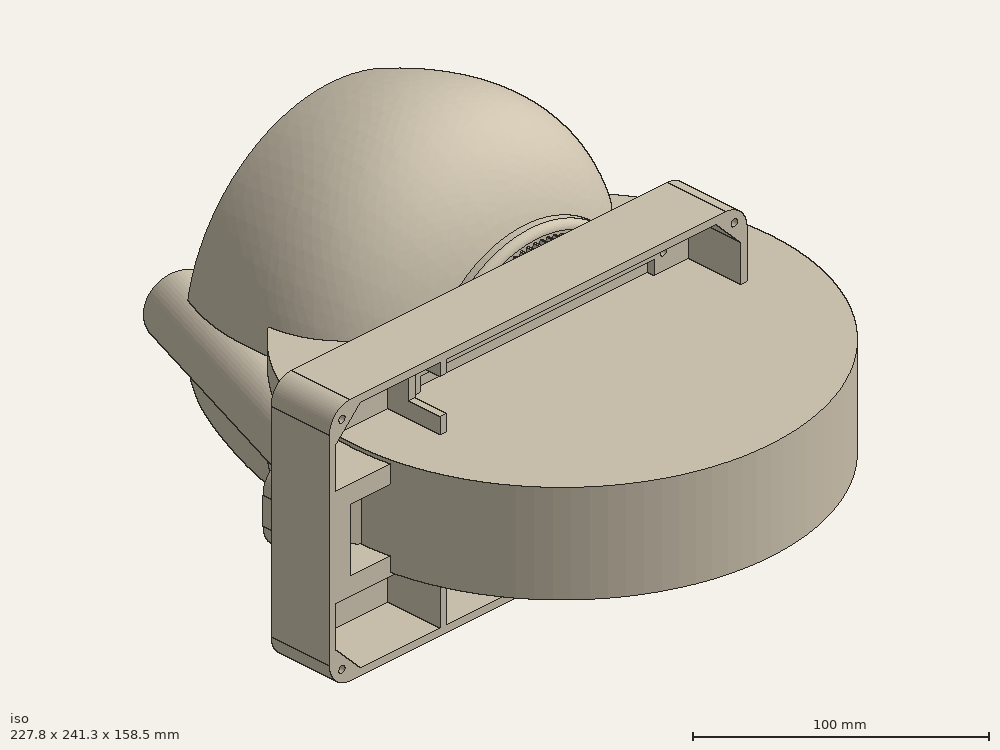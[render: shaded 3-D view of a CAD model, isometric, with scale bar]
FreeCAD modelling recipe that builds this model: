
FCSTD DOCUMENT  (FreeCAD 0.21R33771 (Git))
Label: hello_bowl
License: All rights reserved
LicenseURL: https://en.wikipedia.org/wiki/All_rights_reserved
objects: Sketcher::SketchObject×38, PartDesign::Pocket×19, PartDesign::Pad×17, PartDesign::Body×14, PartDesign::Fillet×12, Mesh::Feature×8, Part::Feature×3, PartDesign::Revolution×2, PartDesign::PolarPattern×2, PartDesign::FeaturePython×2, Part::Part2DObjectPython×1, Part::Cylinder×1, Part::Cut×1
note: 162 computed .brp shape members not serialized (recipe doc carries the construction recipe); baked Part::Feature solids carry a one-line shape summary decoded from their .brp

FEATURE [Mesh::Feature] _  label="2"
  Placement = pos=(-60.5739,41.9909,16.8) rot=(0.990267,0.001215,0.139173;3.15888rad)
FEATURE [Mesh::Feature] _001  label="1"
  Placement = pos=(-57.21,43.02,-7.46) rot=(0,0,1;0rad)
FEATURE [Mesh::Feature] motor
  Placement = pos=(-51.81,-45.18,0) rot=(0,1,0;2.32129rad)
FEATURE [Mesh::Feature] Motor_Gear
  Placement = pos=(-53.5,108.6,-21.24) rot=(0,0,1;0rad)
FEATURE [Mesh::Feature] Base
  Placement = pos=(0,0,0) rot=(1,0,0;3.14159rad)
FEATURE [Mesh::Feature] Top_plate_
  Placement = pos=(9.04249,-243.781,-2.54) rot=(0,0,1;0.087266rad)
FEATURE [Sketcher::SketchObject] Sketch002
  FullyConstrained = true
  MapMode = 5
  Support = -> [XY_Plane001]
  sketch-geometry (1):
    g0: Circle CenterX=0 CenterY=0 CenterZ=0 NormalX=0 NormalY=0 NormalZ=1 AngleXU=0 Radius=100
  constraints (2):
    c: Coincident(g0,g-1)
    c: Diameter(g0) = 200
FEATURE [PartDesign::Pad] Pad001
  Direction = (0,0,1)
  Length = 44
  Length2 = 10
  Profile = -> Sketch002
  ReferenceAxis = -> Sketch002 [N_Axis]
  Type = 0
FEATURE [Sketcher::SketchObject] Sketch003
  FullyConstrained = true
  MapMode = 5
  Support = -> [XY_Plane001]
  sketch-geometry (2):
    g0: Circle CenterX=0 CenterY=0 CenterZ=0 NormalX=0 NormalY=0 NormalZ=1 AngleXU=0 Radius=98.5
    g1: Circle CenterX=0 CenterY=0 CenterZ=0 NormalX=0 NormalY=0 NormalZ=1 AngleXU=0 Radius=10
  constraints (4):
    c: Coincident(g0,g-1)
    c: Diameter(g0) = 197
    c: Coincident(g1,g0)
    c: Diameter(g1) = 20
FEATURE [PartDesign::Pocket] Pocket001
  BaseFeature = -> Pad001
  Direction = (0,0,-1)
  Length = 42
  Length2 = 5
  Profile = -> Sketch003
  ReferenceAxis = -> Sketch003 [N_Axis]
  Reversed = true
  Type = 0
FEATURE [Sketcher::SketchObject] Sketch
  FullyConstrained = true
  MapMode = 5
  Support = -> [XY_Plane001]
  sketch-geometry (2):
    g0: Circle CenterX=0 CenterY=0 CenterZ=0 NormalX=0 NormalY=0 NormalZ=1 AngleXU=0 Radius=10
    g1: Circle CenterX=0 CenterY=0 CenterZ=0 NormalX=0 NormalY=0 NormalZ=1 AngleXU=0 Radius=4
  constraints (4):
    c: Coincident(g0,g-1)
    c: Coincident(g1,g0)
    c: Diameter(g1) = 8
    c: Diameter(g0) = 20
FEATURE [PartDesign::Pocket] Pocket
  BaseFeature = -> Pocket001
  Direction = (0,0,-1)
  Length = 25
  Length2 = 5
  Profile = -> Sketch
  ReferenceAxis = -> Sketch [N_Axis]
  Reversed = true
  Type = 0
FEATURE [PartDesign::Fillet] Fillet
  Base = -> Pocket [Edge7]
  BaseFeature = -> Pocket
  Radius = 7
  SupportTransform = false
  UseAllEdges = false
FEATURE [PartDesign::Fillet] Fillet001
  Base = -> Fillet [Edge10]
  BaseFeature = -> Fillet
  Radius = 3
  SupportTransform = false
  UseAllEdges = false
FEATURE [PartDesign::Fillet] Fillet002
  Base = -> Fillet001 [Edge2]
  BaseFeature = -> Fillet001
  Radius = 1
  SupportTransform = false
  UseAllEdges = false
FEATURE [Sketcher::SketchObject] Sketch004
  AttachmentOffset = pos=(0,0,-89) rot=(0,0,1;0rad)
  FullyConstrained = true
  MapMode = 5
  Placement = pos=(0,89,1.98e-14) rot=(1,0,0;1.5708rad)
  Support = -> [XZ_Plane001]
  sketch-geometry (1):
    g0: Circle CenterX=0 CenterY=35 CenterZ=0 NormalX=0 NormalY=0 NormalZ=1 AngleXU=0 Radius=6
  constraints (3):
    c: PointOnObject(g0,g-2)
    c: Diameter(g0) = 12
    c: DistanceY(g-1,g0) = 35
FEATURE [PartDesign::Pocket] Pocket002
  BaseFeature = -> Fillet002
  Direction = (0,1,2e-16)
  Length = 32
  Length2 = 5
  Profile = -> Sketch004
  ReferenceAxis = -> Sketch004 [N_Axis]
  Type = 0
FEATURE [PartDesign::Body] Body001  label="base body"
  Group = -> [Sketch002,Pad001,Sketch003,Pocket001,Sketch,Pocket,Fillet,Fillet001,Fillet002,Sketch004,Pocket002]
  Origin = -> Origin001
  Placement = pos=(-11.16,-16.75,-20.39) rot=(0,0,1;0rad)
  Tip = -> Pocket002
FEATURE [Sketcher::SketchObject] Sketch005
  AttachmentOffset = pos=(-51.5,0,0) rot=(0,0,1;0rad)
  FullyConstrained = true
  MapMode = 5
  Placement = pos=(-51.5,0,0) rot=(1,0,0;1.5708rad)
  Support = -> [XZ_Plane]
  sketch-geometry (6):
    g0: ArcOfCircle CenterX=0 CenterY=0 CenterZ=0 NormalX=0 NormalY=0 NormalZ=1 AngleXU=0 Radius=22 StartAngle=3.14159 EndAngle=4.16257
    g1: LineSegment StartX=-22 StartY=21.5 StartZ=0 EndX=22 EndY=21.5 EndZ=0
    g2: LineSegment StartX=22 StartY=21.5 StartZ=0 EndX=22 EndY=-7.1e-15 EndZ=0
    g3: LineSegment StartX=-22 StartY=2.7e-15 StartZ=0 EndX=-22 EndY=21.5 EndZ=0
    g4: LineSegment StartX=-11.4957 StartY=-18.7576 StartZ=0 EndX=11.4957 EndY=-18.7576 EndZ=0
    g5: ArcOfCircle CenterX=0 CenterY=0 CenterZ=0 NormalX=0 NormalY=0 NormalZ=1 AngleXU=0 Radius=22 StartAngle=5.26221 EndAngle=6.28319
  constraints (17):
    c: Coincident(g0,g-1)
    c: Diameter(g0) = 44
    c: Coincident(g1,g2)
    c: Coincident(g3,g1)
    c: Vertical(g2)
    c: Vertical(g3)
    c: PointOnObject(g2,g-1)
    c: DistanceY(g3,g3) = 21.5
    c: Coincident(g5,g2)
    c: Block(g0)
    c: Coincident(g3,g0)
    c: Horizontal(g1)
    c: Horizontal(g4)
    c: Equal(g0,g5)
    c: Coincident(g0,g4)
    c: Coincident(g5,g4)
    c: Coincident(g0,g5)
FEATURE [PartDesign::Pad] Pad
  Direction = (0,-1,-2e-16)
  Length = 4
  Length2 = 10
  Placement = pos=(0,0,0) rot=(1,0,0;1.5708rad)
  Profile = -> Sketch005
  ReferenceAxis = -> Sketch005 [N_Axis]
  Reversed = true
  Type = 0
FEATURE [Sketcher::SketchObject] Sketch006
  AttachmentOffset = pos=(-51.9,0,0) rot=(0,0,1;0rad)
  FullyConstrained = false
  MapMode = 5
  Placement = pos=(-51.9,0,0) rot=(1,0,0;1.5708rad)
  Support = -> [XZ_Plane]
  sketch-geometry (6):
    g0: ArcOfCircle CenterX=0 CenterY=0 CenterZ=0 NormalX=0 NormalY=0 NormalZ=1 AngleXU=0 Radius=18.59 StartAngle=0 EndAngle=3.14159
    g1: LineSegment StartX=-21.6 StartY=21.5 StartZ=0 EndX=22.4 EndY=21.5 EndZ=0
    g2: LineSegment StartX=22.4 StartY=21.5 StartZ=0 EndX=22.4 EndY=0 EndZ=0
    g3: LineSegment StartX=22.4 StartY=0 StartZ=0 EndX=18.59 EndY=0 EndZ=0
    g4: LineSegment StartX=-21.6 StartY=0 StartZ=0 EndX=-21.6 EndY=21.5 EndZ=0
    g5: LineSegment StartX=-18.59 StartY=2.3e-15 StartZ=0 EndX=-21.6 EndY=0 EndZ=0
  constraints (18):
    c: Coincident(g0,g-1)
    c: Diameter(g0) = 37.18
    c: Coincident(g1,g2)
    c: Coincident(g2,g3)
    c: Coincident(g5,g4)
    c: Coincident(g4,g1)
    c: Horizontal(g1)
    c: Horizontal(g3)
    c: Vertical(g2)
    c: Vertical(g4)
    c: DistanceX(g1,g1) = 44
    c: PointOnObject(g2,g-1)
    c: Coincident(g3,g0)
    c: Coincident(g5,g0)
    c: Block(g0)
    c: DistanceY(g4,g4) = 21.5
    c: Equal(g2,g4)
    c: DistanceX(g0,g0) = 18.59
FEATURE [PartDesign::Pad] Pad002
  BaseFeature = -> Pad
  Direction = (0,-1,-2e-16)
  Length = 12
  Length2 = 10
  Placement = pos=(0,0,0) rot=(1,0,0;1.5708rad)
  Profile = -> Sketch006
  ReferenceAxis = -> Sketch006 [N_Axis]
  Type = 0
FEATURE [Sketcher::SketchObject] Sketch007
  AttachmentOffset = pos=(-51,0,19.5) rot=(0,0,1;0rad)
  ExternalGeometry = -> [Pad002]
  FullyConstrained = false
  MapMode = 5
  Placement = pos=(-51,0,19.5) rot=(0,0,1;0rad)
  Support = -> [XY_Plane]
  sketch-geometry (6):
    g0: LineSegment StartX=-5.92038 StartY=55 StartZ=0 EndX=4.92038 EndY=55 EndZ=0
    g1: LineSegment StartX=21.5 StartY=38.4204 StartZ=0 EndX=21.5 EndY=0 EndZ=0
    g2: LineSegment StartX=21.5 StartY=0 StartZ=0 EndX=-22.5 EndY=0 EndZ=0
    g3: LineSegment StartX=-22.5 StartY=0 StartZ=0 EndX=-22.5 EndY=38.4204 EndZ=0
    g4: ArcOfCircle CenterX=-5.92038 CenterY=38.4204 CenterZ=0 NormalX=0 NormalY=0 NormalZ=1 AngleXU=0 Radius=16.5796 StartAngle=1.5708 EndAngle=3.14159
    g5: ArcOfCircle CenterX=4.92038 CenterY=38.4204 CenterZ=0 NormalX=0 NormalY=0 NormalZ=1 AngleXU=0 Radius=16.5796 StartAngle=0 EndAngle=1.5708
  constraints (14):
    c: Coincident(g1,g2)
    c: Coincident(g2,g3)
    c: Horizontal(g0)
    c: Horizontal(g2)
    c: Vertical(g1)
    c: Vertical(g3)
    c: Tangent(g0,g4) = 1.5708
    c: Tangent(g3,g4) = 1.5708
    c: Tangent(g0,g5) = 1.5708
    c: Tangent(g1,g5) = 1.5708
    c: Equal(g3,g1)
    c: DistanceX(g2,g2) = 44
    c: DistanceY(g2,g0) = 55
    c: Coincident(g-4,g2)
FEATURE [PartDesign::Pad] Pad003  label="bottom"
  BaseFeature = -> Pad002
  Direction = (0,0,1)
  Length = 2
  Length2 = 10
  Placement = pos=(0,0,0) rot=(1,0,0;1.5708rad)
  Profile = -> Sketch007
  ReferenceAxis = -> Sketch007 [N_Axis]
  Type = 0
FEATURE [Sketcher::SketchObject] Sketch008
  AttachmentOffset = pos=(-52,0,-2.5) rot=(0,0,1;0rad)
  FullyConstrained = true
  MapMode = 5
  Placement = pos=(-52,0,-2.5) rot=(0,0,1;0rad)
  Support = -> [XY_Plane]
  sketch-geometry (1):
    g0: Circle CenterX=-5.24 CenterY=43 CenterZ=0 NormalX=0 NormalY=0 NormalZ=1 AngleXU=0 Radius=6
  constraints (3):
    c: Diameter(g0) = 12
    c: DistanceY(g-1,g0) = 43
    c: DistanceX(g0,g-1) = 5.24
FEATURE [PartDesign::Pad] Pad004
  BaseFeature = -> Pad003
  Direction = (0,0,1)
  Length = 24
  Length2 = 10
  Placement = pos=(0,0,0) rot=(1,0,0;1.5708rad)
  Profile = -> Sketch008
  ReferenceAxis = -> Sketch008 [N_Axis]
  Type = 0
FEATURE [Sketcher::SketchObject] Sketch009
  ExternalGeometry = -> [Pad004]
  FullyConstrained = true
  MapMode = 5
  Support = -> [XY_Plane]
  sketch-geometry (1):
    g0: Circle CenterX=-57.24 CenterY=43 CenterZ=0 NormalX=0 NormalY=0 NormalZ=1 AngleXU=0 Radius=1.55
  constraints (2):
    c: Diameter(g0) = 3.1
    c: Block(g0)
FEATURE [PartDesign::Pad] Pad005
  BaseFeature = -> Pad004
  Direction = (0,0,1)
  Length = 19.4
  Length2 = 10
  Placement = pos=(0,0,0) rot=(1,0,0;1.5708rad)
  Profile = -> Sketch009
  ReferenceAxis = -> Sketch009 [N_Axis]
  Reversed = true
  Type = 0
FEATURE [Part::Feature] Part__Feature  label="Orange-Johnson motor 12V 300 RPM Grade-A"
  Placement = pos=(-51.9475,-22.8102,-0.18599) rot=(-0.30964,0.669154,0.675541;2.55272rad)
  shape: bbox 37.25 x 108.6 x 37.1 mm, 69 faces (baked)
FEATURE [Sketcher::SketchObject] Sketch010
  AttachmentOffset = pos=(-52,-1,0) rot=(0,0,1;0rad)
  FullyConstrained = false
  MapMode = 5
  Placement = pos=(-52,2e-16,-1) rot=(1,0,0;1.5708rad)
  Support = -> [XZ_Plane]
  sketch-geometry (4):
    g0: Circle CenterX=-15.164 CenterY=4.14914 CenterZ=0 NormalX=0 NormalY=0 NormalZ=1 AngleXU=0 Radius=1.75
    g1: Circle CenterX=10.2205 CenterY=12.9017 CenterZ=0 NormalX=0 NormalY=0 NormalZ=1 AngleXU=0 Radius=1.75
    g2: Circle CenterX=5.1073 CenterY=-13.4573 CenterZ=0 NormalX=0 NormalY=0 NormalZ=1 AngleXU=0 Radius=1.75
    g3: Circle CenterX=-5.24 CenterY=5.77466 CenterZ=0 NormalX=0 NormalY=0 NormalZ=1 AngleXU=0 Radius=6.75
  constraints (8):
    c: Diameter(g2) = 3.5
    c: Diameter(g1) = 3.5
    c: Diameter(g0) = 3.5
    c: Block(g1)
    c: Block(g2)
    c: Block(g0)
    c: DistanceX(g3,g-1) = 5.24
    c: Diameter(g3) = 13.5
FEATURE [PartDesign::Pocket] Pocket003
  BaseFeature = -> Pad005
  Direction = (0,1,2e-16)
  Length = 10
  Length2 = 5
  Placement = pos=(0,0,0) rot=(1,0,0;1.5708rad)
  Profile = -> Sketch010
  ReferenceAxis = -> Sketch010 [N_Axis]
  Type = 0
FEATURE [Sketcher::SketchObject] Sketch011
  FullyConstrained = true
  MapMode = 5
  Support = -> [XY_Plane002]
  sketch-geometry (4):
    g0: LineSegment StartX=-13 StartY=37 StartZ=0 EndX=13 EndY=37 EndZ=0
    g1: LineSegment StartX=13 StartY=37 StartZ=0 EndX=13 EndY=0 EndZ=0
    g2: LineSegment StartX=13 StartY=0 StartZ=0 EndX=-13 EndY=0 EndZ=0
    g3: LineSegment StartX=-13 StartY=0 StartZ=0 EndX=-13 EndY=37 EndZ=0
  constraints (11):
    c: Coincident(g0,g1)
    c: Coincident(g1,g2)
    c: Coincident(g2,g3)
    c: Coincident(g3,g0)
    c: Horizontal(g0)
    c: Horizontal(g2)
    c: Vertical(g1)
    c: Vertical(g3)
    c: DistanceY(g3,g3) = 37
    c: DistanceX(g2,g2) = 26
    c: Symmetric(g2,g1,g-1)
FEATURE [Sketcher::SketchObject] Sketch001
  FullyConstrained = true
  MapMode = 5
  Support = -> [XY_Plane002]
  sketch-geometry (10):
    g0: ArcOfCircle CenterX=-0.294523 CenterY=40.7886 CenterZ=0 NormalX=0 NormalY=0 NormalZ=1 AngleXU=0 Radius=3.8 StartAngle=2.61452 EndAngle=4.78997
    g1: ArcOfCircle CenterX=-0.294523 CenterY=40.7886 CenterZ=0 NormalX=0 NormalY=0 NormalZ=1 AngleXU=0 Radius=5.5 StartAngle=2.78665 EndAngle=4.19811
    g2: LineSegment StartX=-13 StartY=0 StartZ=0 EndX=-13 EndY=2 EndZ=0
    g3: LineSegment StartX=-13 StartY=2 StartZ=0 EndX=-3 EndY=2 EndZ=0
    g4: LineSegment StartX=-3 StartY=2 StartZ=0 EndX=-3 EndY=36 EndZ=0
    g5: LineSegment StartX=0 StartY=0 StartZ=0 EndX=-13 EndY=0 EndZ=0
    g6: LineSegment StartX=0 StartY=37 StartZ=0 EndX=0 EndY=0 EndZ=0
    g7: LineSegment StartX=-5.4517 StartY=42.7 StartZ=0 EndX=-3.57879 EndY=42.7 EndZ=0
    g8: LineSegment StartX=0 StartY=37 StartZ=0 EndX=0 EndY=0 EndZ=0
    g9: LineSegment StartX=0 StartY=37 StartZ=0 EndX=0 EndY=0 EndZ=0
  constraints (28):
    c: Diameter(g0) = 7.6
    c: Coincident(g1,g0)
    c: Diameter(g1) = 11
    c: Vertical(g2)
    c: Coincident(g2,g3)
    c: Horizontal(g3)
    c: Coincident(g3,g4)
    c: Vertical(g4)
    c: Coincident(g5,g-1)
    c: Coincident(g5,g2)
    c: Coincident(g6,g5)
    c: Vertical(g6)
    c: Coincident(g6,g0)
    c: DistanceY(g2,g2) = 2
    c: Coincident(g4,g1)
    c: Coincident(g7,g1)
    c: Coincident(g7,g0)
    c: Horizontal(g7)
    c: Coincident(g8,g0)
    c: Coincident(g8,g5)
    c: DistanceY(g4,g4) = 34
    c: Horizontal(g5)
    c: Coincident(g9,g0)
    c: Coincident(g9,g5)
    c: DistanceY(g1,g0) = 1
    c: DistanceX(g1,g0) = 3
    c: DistanceY(g0,g0) = 5.7
    c: DistanceX(g5,g5) = 13
FEATURE [PartDesign::Revolution] Revolution
  Angle = 360
  Axis = (0,1,0)
  Base = (0,0,0)
  Profile = -> Sketch001
  ReferenceAxis = -> Sketch001 [V_Axis]
FEATURE [PartDesign::Fillet] Fillet005
  Base = -> Revolution [Edge9]
  BaseFeature = -> Revolution
  Radius = 11
  SupportTransform = false
  UseAllEdges = false
FEATURE [PartDesign::Fillet] Fillet006
  Base = -> Fillet005 [Edge3]
  BaseFeature = -> Fillet005
  Radius = 9.9
  SupportTransform = false
  UseAllEdges = false
FEATURE [PartDesign::Body] Body002  label="support structures"
  Group = -> [Sketch011,Sketch001,Revolution,Fillet005,Fillet006]
  Origin = -> Origin002
  Placement = pos=(37.62,5e-15,21.6) rot=(-1,0,0;1.5708rad)
  Tip = -> Fillet006
FEATURE [Part::Part2DObjectPython] InvoluteGear  # Draft 2D object (typed FeaturePython)
  AddendumCoefficient = 1
  DedendumCoefficient = 1.35
  ExternalGear = true
  HighPrecision = true
  Modules = 2.03
  NumberOfTeeth = 15
  PressureAngle = 20
  ProfileShiftCoefficient = 0
  RootFilletCoefficient = 0
FEATURE [PartDesign::Pad] Pad006
  Direction = (0,0,1)
  Length = 10
  Length2 = 10
  Profile = -> InvoluteGear
  ReferenceAxis = -> InvoluteGear [N_Axis]
  Reversed = true
  Type = 0
FEATURE [Sketcher::SketchObject] Sketch012
  FullyConstrained = true
  MapMode = 5
  Support = -> [XY_Plane003]
  sketch-geometry (1):
    g0: Circle CenterX=0 CenterY=0 CenterZ=0 NormalX=0 NormalY=0 NormalZ=1 AngleXU=0 Radius=5
  constraints (2):
    c: Coincident(g0,g-1)
    c: Diameter(g0) = 10
FEATURE [PartDesign::Pocket] Pocket004
  BaseFeature = -> Pad006
  Direction = (0,0,-1)
  Length = 5
  Length2 = 5
  Profile = -> Sketch012
  ReferenceAxis = -> Sketch012 [N_Axis]
  Type = 1
FEATURE [PartDesign::Body] Body003  label="motor_gear"
  Group = -> [InvoluteGear,Pad006,Sketch012,Pocket004]
  Origin = -> Origin003
  Placement = pos=(-57.21,43,-11.24) rot=(0,0,1;0rad)
  Tip = -> Pocket004
FEATURE [Part::Feature] _002  label="motor_bevel_gear_02"
  shape: bbox 43.04 x 43.04 x 10.6 mm, 17106 faces, 0 solids (baked)
FEATURE [PartDesign::Fillet] Fillet007
  Base = -> Pocket003 [Edge69]
  BaseFeature = -> Pocket003
  Placement = pos=(0,0,0) rot=(1,0,0;1.5708rad)
  Radius = 2
  SupportTransform = false
  UseAllEdges = false
FEATURE [PartDesign::Body] Body  label="motor support"
  Group = -> [Sketch005,Pad,Sketch006,Pad002,Sketch007,Pad003,Sketch008,Pad004,Sketch009,Pad005,Sketch010,Pocket003,Fillet007]
  Origin = -> Origin
  Tip = -> Fillet007
FEATURE [Part::Feature] _002_solid  label="motor_bevel_gear_02 (Solid)"
  shape: bbox 43.04 x 43.04 x 10.6 mm, 17106 faces (baked)
FEATURE [Part::Cylinder] Cylinder
  Angle = 360
  AttacherType = Attacher::AttachEngine3D
  FirstAngle = 0
  Height = 10
  Placement = pos=(-57.23,43.01,-11.99) rot=(0,0,1;0rad)
  Radius = 5
  SecondAngle = 0
FEATURE [Part::Cut] Cut
  Base = -> _002_solid
  Tool = -> Cylinder
FEATURE [Mesh::Feature] mount_bracket
FEATURE [Mesh::Feature] new_mount
FEATURE [Sketcher::SketchObject] Sketch016
  FullyConstrained = true
  MapMode = 5
  Placement = pos=(0,0,0) rot=(1,0,0;1.5708rad)
  Support = -> [XZ_Plane005]
  sketch-geometry (2):
    g0: Circle CenterX=0 CenterY=0 CenterZ=0 NormalX=0 NormalY=0 NormalZ=1 AngleXU=0 Radius=18.5
    g1: Circle CenterX=0 CenterY=0 CenterZ=0 NormalX=0 NormalY=0 NormalZ=1 AngleXU=0 Radius=10
  constraints (4):
    c: Diameter(g0) = 37
    c: Diameter(g1) = 20
    c: Coincident(g0,g1)
    c: Coincident(g0,g-1)
FEATURE [PartDesign::Pad] Pad010
  Direction = (0,-1,2e-16)
  Length = 9
  Length2 = 10
  Placement = pos=(0,0,0) rot=(1,0,0;1.5708rad)
  Profile = -> Sketch016
  ReferenceAxis = -> Sketch016 [N_Axis]
  Reversed = true
  Type = 0
FEATURE [PartDesign::Fillet] Fillet010
  Base = -> Pad010 [Edge3]
  BaseFeature = -> Pad010
  Placement = pos=(0,0,0) rot=(1,0,0;1.5708rad)
  Radius = 0.5
  SupportTransform = false
  UseAllEdges = false
FEATURE [PartDesign::Fillet] Fillet011
  Base = -> Fillet010 [Edge3]
  BaseFeature = -> Fillet010
  Placement = pos=(0,0,0) rot=(1,0,0;1.5708rad)
  Radius = 0.5
  SupportTransform = false
  UseAllEdges = false
FEATURE [PartDesign::Body] Body005  label="large_ball_bearing"
  Group = -> [Sketch016,Pad010,Fillet010,Fillet011]
  Origin = -> Origin005
  Placement = pos=(2.81,1,0) rot=(0,0,1;0rad)
  Tip = -> Fillet011
FEATURE [Sketcher::SketchObject] Sketch020
  FullyConstrained = true
  MapMode = 5
  Support = -> [XY_Plane007]
  sketch-geometry (1):
    g0: Circle CenterX=0 CenterY=0 CenterZ=0 NormalX=0 NormalY=0 NormalZ=1 AngleXU=0 Radius=50
  constraints (2):
    c: Coincident(g0,g-1)
    c: Diameter(g0) = 100
FEATURE [PartDesign::Pad] Pad013
  Direction = (0,0,1)
  Length = 6
  Length2 = 10
  Profile = -> Sketch020
  ReferenceAxis = -> Sketch020 [N_Axis]
  Reversed = true
  Type = 0
FEATURE [Sketcher::SketchObject] Sketch022
  FullyConstrained = true
  MapMode = 5
  Support = -> [XY_Plane008]
  sketch-geometry (1):
    g0: Circle CenterX=0 CenterY=0 CenterZ=0 NormalX=0 NormalY=0 NormalZ=1 AngleXU=0 Radius=3.1
  constraints (2):
    c: Coincident(g0,g-1)
    c: Diameter(g0) = 6.2
FEATURE [Sketcher::SketchObject] Sketch023
  FullyConstrained = true
  MapMode = 5
  Placement = pos=(0,0,0) rot=(1,0,0;1.5708rad)
  Support = -> [XZ_Plane009]
  sketch-geometry (1):
    g0: Circle CenterX=-50 CenterY=0 CenterZ=0 NormalX=0 NormalY=0 NormalZ=1 AngleXU=0 Radius=16.35
  constraints (3):
    c: PointOnObject(g0,g-1)
    c: Diameter(g0) = 32.7
    c: DistanceX(g0,g-1) = 50
FEATURE [PartDesign::Pad] Pad014
  Direction = (0,-1,2e-16)
  Length = 22.6
  Length2 = 10
  Placement = pos=(0,0,0) rot=(1,0,0;1.5708rad)
  Profile = -> Sketch023
  ReferenceAxis = -> Sketch023 [N_Axis]
  Type = 0
FEATURE [Sketcher::SketchObject] Sketch024
  ExternalGeometry = -> [Pad014]
  FullyConstrained = true
  MapMode = 5
  Placement = pos=(0,0,0) rot=(1,0,0;1.5708rad)
  Support = -> [XZ_Plane009]
  sketch-geometry (1):
    g0: Circle CenterX=-50 CenterY=13 CenterZ=0 NormalX=0 NormalY=0 NormalZ=1 AngleXU=0 Radius=1
  constraints (3):
    c: Vertical(g0,g-3)
    c: Diameter(g0) = 2
    c: DistanceY(g-3,g0) = 13
FEATURE [PartDesign::Pocket] Pocket007
  BaseFeature = -> Pad014
  Direction = (0,1,-2e-16)
  Length = 5
  Length2 = 5
  Placement = pos=(0,0,0) rot=(1,0,0;1.5708rad)
  Profile = -> Sketch024
  ReferenceAxis = -> Sketch024 [N_Axis]
  Reversed = true
  Type = 0
FEATURE [PartDesign::PolarPattern] PolarPattern
  Angle = 360
  Axis = -> Pocket007 [Edge2]
  BaseFeature = -> Pocket007
  Occurrences = 6
  Originals = -> [Pocket007]
  Placement = pos=(0,0,0) rot=(1,0,0;1.5708rad)
FEATURE [PartDesign::Body] Body009  label="mini_motor"
  Group = -> [Sketch023,Pad014,Sketch024,Pocket007,PolarPattern]
  Origin = -> Origin009
  Placement = pos=(0.07,1.14,0) rot=(0,0,1;0rad)
  Tip = -> PolarPattern
FEATURE [Sketcher::SketchObject] Sketch025
  FullyConstrained = false
  MapMode = 5
  Placement = pos=(0,0,0) rot=(1,0,0;1.5708rad)
  Support = -> [XZ_Plane010]
  sketch-geometry (7):
    g0: LineSegment StartX=-80 StartY=35 StartZ=0 EndX=50 EndY=35 EndZ=0
    g1: LineSegment StartX=50 StartY=35 StartZ=0 EndX=50 EndY=-35 EndZ=0
    g2: LineSegment StartX=50 StartY=-35 StartZ=0 EndX=-80 EndY=-35 EndZ=0
    g3: LineSegment StartX=-80 StartY=-35 StartZ=0 EndX=-80 EndY=35 EndZ=0
    g4: Circle CenterX=-50 CenterY=0 CenterZ=0 NormalX=0 NormalY=0 NormalZ=1 AngleXU=0 Radius=18.6
    g5: Circle CenterX=-50 CenterY=22 CenterZ=0 NormalX=0 NormalY=0 NormalZ=1 AngleXU=0 Radius=1.5
    g6: Circle CenterX=-50 CenterY=-22 CenterZ=0 NormalX=0 NormalY=0 NormalZ=1 AngleXU=0 Radius=1.5
  constraints (20):
    c: Coincident(g0,g1)
    c: Coincident(g1,g2)
    c: Coincident(g2,g3)
    c: Coincident(g3,g0)
    c: Horizontal(g0)
    c: Horizontal(g2)
    c: Vertical(g1)
    c: Vertical(g3)
    c: DistanceY(g-1,g0) = 35
    c: DistanceY(g1,g-1) = 35
    c: PointOnObject(g4,g-1)
    c: Diameter(g4) = 37.2
    c: Equal(g6,g5)
    c: Diameter(g5) = 3
    c: Vertical(g6,g4)
    c: Vertical(g4,g5)
    c: DistanceY(g4,g5) = 22
    c: DistanceY(g6,g4) = 22
    c: DistanceX(g0,g0) = 130
    c: DistanceX(g0,g-1) = 80
FEATURE [PartDesign::Pad] Pad015
  Direction = (0,-1,-2e-16)
  Length = 5
  Length2 = 10
  Placement = pos=(0,0,0) rot=(1,0,0;1.5708rad)
  Profile = -> Sketch025
  ReferenceAxis = -> Sketch025 [N_Axis]
  Type = 0
FEATURE [Sketcher::SketchObject] Sketch028
  FullyConstrained = true
  MapMode = 5
  Placement = pos=(0,0,0) rot=(1,0,0;1.5708rad)
  Support = -> [XZ_Plane010]
  sketch-geometry (1):
    g0: Circle CenterX=-50 CenterY=13 CenterZ=0 NormalX=0 NormalY=0 NormalZ=1 AngleXU=0 Radius=1
  constraints (3):
    c: DistanceX(g0,g-1) = 50
    c: Diameter(g0) = 2
    c: DistanceY(g-1,g0) = 13
FEATURE [PartDesign::Pocket] Pocket009
  BaseFeature = -> Pad015
  Direction = (0,1,2e-16)
  Length = 6
  Length2 = 5
  Placement = pos=(0,0,0) rot=(1,0,0;1.5708rad)
  Profile = -> Sketch028
  ReferenceAxis = -> Sketch028 [N_Axis]
  Type = 0
FEATURE [Sketcher::SketchObject] Sketch029
  FullyConstrained = false
  MapMode = 5
  Placement = pos=(0,0,0) rot=(1,0,0;1.5708rad)
  Support = -> [XZ_Plane010]
  sketch-geometry (1):
    g0: Circle CenterX=2.75243 CenterY=0 CenterZ=0 NormalX=0 NormalY=0 NormalZ=1 AngleXU=0 Radius=12
  constraints (2):
    c: Diameter(g0) = 24
    c: PointOnObject(g0,g-1)
FEATURE [PartDesign::Pad] Pad017
  BaseFeature = -> Pocket009
  Direction = (0,-1,-2e-16)
  Length = 2
  Length2 = 10
  Placement = pos=(0,0,0) rot=(1,0,0;1.5708rad)
  Profile = -> Sketch029
  ReferenceAxis = -> Sketch029 [N_Axis]
  Reversed = true
  Type = 0
FEATURE [Sketcher::SketchObject] Sketch030
  ExternalGeometry = -> [Pad017]
  FullyConstrained = true
  MapMode = 5
  Placement = pos=(0,0,0) rot=(1,0,0;1.5708rad)
  Support = -> [XZ_Plane010]
  sketch-geometry (1):
    g0: Circle CenterX=2.75243 CenterY=0 CenterZ=0 NormalX=0 NormalY=0 NormalZ=1 AngleXU=0 Radius=10
  constraints (2):
    c: Diameter(g0) = 20
    c: Coincident(g0,g-3)
FEATURE [PartDesign::Pad] Pad018
  BaseFeature = -> Pad017
  Direction = (0,-1,-2e-16)
  Length = 8
  Length2 = 10
  Placement = pos=(0,0,0) rot=(1,0,0;1.5708rad)
  Profile = -> Sketch030
  ReferenceAxis = -> Sketch030 [N_Axis]
  Reversed = true
  Type = 0
FEATURE [Sketcher::SketchObject] Sketch031
  ExternalGeometry = -> [Pad018]
  FullyConstrained = true
  MapMode = 5
  Placement = pos=(0,0,0) rot=(1,0,0;1.5708rad)
  Support = -> [XZ_Plane010]
  sketch-geometry (4):
    g0: Circle CenterX=-76 CenterY=31 CenterZ=0 NormalX=0 NormalY=0 NormalZ=1 AngleXU=0 Radius=1.5
    g1: Circle CenterX=-76 CenterY=-31 CenterZ=0 NormalX=0 NormalY=0 NormalZ=1 AngleXU=0 Radius=1.5
    g2: Circle CenterX=46 CenterY=31 CenterZ=0 NormalX=0 NormalY=0 NormalZ=1 AngleXU=0 Radius=1.5
    g3: Circle CenterX=46 CenterY=-31 CenterZ=0 NormalX=0 NormalY=0 NormalZ=1 AngleXU=0 Radius=1.5
  constraints (12):
    c: Diameter(g3) = 3
    c: Diameter(g2) = 3
    c: Diameter(g0) = 3
    c: Diameter(g1) = 3
    c: Horizontal(g0,g2)
    c: Horizontal(g1,g3)
    c: Vertical(g1,g0)
    c: Vertical(g3,g2)
    c: DistanceX(g-3,g0) = 4
    c: DistanceY(g0,g-3) = 4
    c: DistanceY(g-3,g1) = 4
    c: DistanceX(g3,g-4) = 4
FEATURE [PartDesign::Pocket] Pocket010
  BaseFeature = -> Pad018
  Direction = (0,1,2e-16)
  Length = 5
  Length2 = 5
  Placement = pos=(0,0,0) rot=(1,0,0;1.5708rad)
  Profile = -> Sketch031
  ReferenceAxis = -> Sketch031 [N_Axis]
  Reversed = true
  Type = 1
FEATURE [Sketcher::SketchObject] Sketch034
  FullyConstrained = true
  MapMode = 5
  Placement = pos=(0,0,0) rot=(1,0,0;1.5708rad)
  Support = -> [XZ_Plane012]
  sketch-geometry (4):
    g0: Circle CenterX=-50 CenterY=0 CenterZ=0 NormalX=0 NormalY=0 NormalZ=1 AngleXU=0 Radius=24
    g1: Circle CenterX=-50 CenterY=22 CenterZ=0 NormalX=0 NormalY=0 NormalZ=1 AngleXU=0 Radius=1.5
    g2: Circle CenterX=-50 CenterY=-22 CenterZ=0 NormalX=0 NormalY=0 NormalZ=1 AngleXU=0 Radius=1.5
    g3: Circle CenterX=-50 CenterY=0 CenterZ=0 NormalX=0 NormalY=0 NormalZ=1 AngleXU=0 Radius=5
  constraints (11):
    c: PointOnObject(g0,g-1)
    c: Diameter(g0) = 48
    c: DistanceX(g0,g-1) = 50
    c: Diameter(g2) = 3
    c: Equal(g1,g2)
    c: Coincident(g3,g0)
    c: Diameter(g3) = 10
    c: DistanceY(g0,g1) = 22
    c: DistanceY(g2,g0) = 22
    c: Vertical(g2,g0)
    c: Vertical(g0,g1)
FEATURE [PartDesign::Pad] Pad021
  Direction = (0,-1,-2e-16)
  Length = 2
  Length2 = 10
  Placement = pos=(0,0,0) rot=(1,0,0;1.5708rad)
  Profile = -> Sketch034
  ReferenceAxis = -> Sketch034 [N_Axis]
  Reversed = true
  Type = 0
FEATURE [Sketcher::SketchObject] Sketch036
  FullyConstrained = true
  MapMode = 5
  Placement = pos=(0,0,0) rot=(1,0,0;1.5708rad)
  Support = -> [XZ_Plane012]
  sketch-geometry (1):
    g0: Circle CenterX=-50 CenterY=13 CenterZ=0 NormalX=0 NormalY=0 NormalZ=1 AngleXU=0 Radius=1
  constraints (3):
    c: DistanceX(g0,g-1) = 50
    c: Diameter(g0) = 2
    c: DistanceY(g-1,g0) = 13
FEATURE [PartDesign::Pocket] Pocket012
  BaseFeature = -> Pad021
  Direction = (0,1,2e-16)
  Length = 6
  Length2 = 5
  Placement = pos=(0,0,0) rot=(1,0,0;1.5708rad)
  Profile = -> Sketch036
  ReferenceAxis = -> Sketch036 [N_Axis]
  Type = 0
FEATURE [PartDesign::PolarPattern] PolarPattern002
  Angle = 360
  Axis = -> Pocket012 [Edge3]
  BaseFeature = -> Pocket012
  Occurrences = 6
  Originals = -> [Pocket012]
  Placement = pos=(0,0,0) rot=(1,0,0;1.5708rad)
FEATURE [PartDesign::Body] Body012  label="motor_holder"
  Group = -> [Sketch034,Pad021,Sketch036,Pocket012,PolarPattern002]
  Origin = -> Origin012
  Tip = -> PolarPattern002
FEATURE [PartDesign::Fillet] Fillet017
  Base = -> Pocket010 [Edge1,Edge5,Edge2,Edge8]
  BaseFeature = -> Pocket010
  Placement = pos=(0,0,0) rot=(1,0,0;1.5708rad)
  Radius = 4
  SupportTransform = false
  UseAllEdges = false
FEATURE [PartDesign::Body] Body010  label="bowl_container_top"
  Group = -> [Sketch025,Pad015,Sketch028,Pocket009,Sketch029,Pad017,Sketch030,Pad018,Sketch031,Pocket010,Fillet017]
  Origin = -> Origin010
  Tip = -> Fillet017
FEATURE [PartDesign::FeaturePython] InvoluteGear001  # WARN: FeaturePython — macro-defined, semantics opaque (R4)
  AttacherType = Attacher::AttachEngine3D
  BaseFeature = -> Pad013
  addendum_diameter = 92
  angular_backlash = 0
  axle_hole = false
  axle_holesize = 10
  backlash = 0
  clearance = 0.25
  double_helix = false
  head = 0
  head_fillet = 0
  height = 5
  helix_angle = 0
  module = 1
  num_teeth = 90
  numpoints = 20
  offset_hole = false
  offset_holeoffset = 10
  offset_holesize = 10
  pitch_diameter = 90
  pressure_angle = 20
  properties_from_tool = false
  reversed_backlash = false
  root_diameter = 87.5
  root_fillet = 0
  shift = 0
  simple = false
  transverse_pitch = 3.14159
  traverse_module = 1
  undercut = false
  version = 1.3.0
  expr: angular_backlash = backlash / pitch_diameter * 360 ° / pi
FEATURE [Sketcher::SketchObject] Sketch021
  FullyConstrained = true
  MapMode = 5
  Support = -> [XY_Plane007]
  sketch-geometry (1):
    g0: Circle CenterX=0 CenterY=0 CenterZ=0 NormalX=0 NormalY=0 NormalZ=1 AngleXU=0 Radius=18.5
  constraints (2):
    c: Coincident(g0,g-1)
    c: Diameter(g0) = 37
FEATURE [PartDesign::Pocket] Pocket014
  BaseFeature = -> InvoluteGear001
  Direction = (0,0,-1)
  Length = 0
  Length2 = 5
  Profile = -> Sketch021
  ReferenceAxis = -> Sketch021 [N_Axis]
  Type = 3
  UpToFace = -> InvoluteGear001 [Face364]
FEATURE [PartDesign::FeaturePython] InvoluteGear002  # WARN: FeaturePython — macro-defined, semantics opaque (R4)
  AttacherType = Attacher::AttachEngine3D
  addendum_diameter = 17
  angular_backlash = 0
  axle_hole = false
  axle_holesize = 10
  backlash = 0
  clearance = 0.25
  double_helix = false
  head = 0
  head_fillet = 0
  height = 5
  helix_angle = 0
  module = 1
  num_teeth = 15
  numpoints = 20
  offset_hole = false
  offset_holeoffset = 10
  offset_holesize = 10
  pitch_diameter = 15
  pressure_angle = 20
  properties_from_tool = false
  reversed_backlash = false
  root_diameter = 12.5
  root_fillet = 0
  shift = 0
  simple = false
  transverse_pitch = 3.14159
  traverse_module = 1
  undercut = false
  version = 1.3.0
  expr: angular_backlash = backlash / pitch_diameter * 360 ° / pi
FEATURE [PartDesign::Pocket] Pocket015
  BaseFeature = -> InvoluteGear002
  Direction = (0,0,-1)
  Length = 5
  Length2 = 5
  Profile = -> Sketch022
  ReferenceAxis = -> Sketch022 [N_Axis]
  Reversed = true
  Type = 1
FEATURE [PartDesign::Body] Body008  label="small_gear"
  Group = -> [Sketch022,InvoluteGear002,Pocket015]
  Origin = -> Origin008
  Placement = pos=(-49.95,3.05998,0.0106814) rot=(-1,0,0;1.56731rad)
  Tip = -> Pocket015
FEATURE [PartDesign::Fillet] Fillet018
  Base = -> Pocket014 [Edge2]
  BaseFeature = -> Pocket014
  Radius = 3
  SupportTransform = false
  UseAllEdges = false
FEATURE [PartDesign::Body] Body007  label="large_gear_and_holder"
  Group = -> [Sketch020,Pad013,Sketch021,InvoluteGear001,Pocket014,Fillet018]
  Origin = -> Origin007
  Placement = pos=(2.76007,8.72995,-0.0293578) rot=(0,-0.705872,0.70834;3.14159rad)
  Tip = -> Fillet018
FEATURE [Sketcher::SketchObject] Sketch038
  FullyConstrained = false
  MapMode = 5
  Support = -> [XY_Plane013]
  sketch-geometry (16):
    g0: Circle CenterX=-35.8872 CenterY=15.6206 CenterZ=0 NormalX=0 NormalY=0 NormalZ=1 AngleXU=0 Radius=1
    g1: Circle CenterX=-104.017 CenterY=21.5521 CenterZ=0 NormalX=0 NormalY=0 NormalZ=1 AngleXU=0 Radius=1
    g2: Circle CenterX=-70 CenterY=105 CenterZ=0 NormalX=0 NormalY=0 NormalZ=1 AngleXU=0 Radius=1
    g3: BSplineCurve PolesCount=4 KnotsCount=2 Degree=3 IsPeriodic=0
    g4: GeomPoint X=0 Y=15 Z=0
    g5: GeomPoint X=-70 Y=105 Z=0
    g6: LineSegment StartX=-70 StartY=105 StartZ=0 EndX=-64.1737 EndY=105 EndZ=0
    g7: LineSegment StartX=-64.1737 StartY=105 StartZ=0 EndX=-70.6315 EndY=87.6601 EndZ=0
    g8: LineSegment StartX=-70.6315 StartY=87.6601 StartZ=0 EndX=-74.4474 EndY=66.8192 EndZ=0
    g9: LineSegment StartX=-74.4474 StartY=66.8192 StartZ=0 EndX=-68.8703 EndY=44.2171 EndZ=0
    g10: LineSegment StartX=-68.8703 StartY=44.2171 StartZ=0 EndX=-59.7707 EndY=35.9982 EndZ=0
    g11: LineSegment StartX=-59.7707 StartY=35.9982 StartZ=0 EndX=-47.4423 EndY=29.834 EndZ=0
    g12: LineSegment StartX=-47.4423 StartY=29.834 StartZ=0 EndX=-24.8402 EndY=23.0827 EndZ=0
    g13: LineSegment StartX=-24.8402 StartY=23.0827 StartZ=0 EndX=-13.3924 EndY=22.4956 EndZ=0
    g14: LineSegment StartX=-13.3924 StartY=22.4956 StartZ=0 EndX=0 EndY=21.9086 EndZ=0
    g15: LineSegment StartX=0 StartY=21.9086 StartZ=0 EndX=0 EndY=15 EndZ=0
  constraints (21):
    c: InternalAlignment(g0,g3)
    c: InternalAlignment(g1,g3)
    c: InternalAlignment(g2,g3)
    c: InternalAlignment(g4,g3)
    c: InternalAlignment(g5,g3)
    c: DistanceY(g3,g3) = 90
    c: DistanceY(g-1,g3) = 15
    c: Coincident(g6,g3)
    c: Horizontal(g6)
    c: Coincident(g6,g7)
    c: Coincident(g7,g8)
    c: Coincident(g8,g9)
    c: Coincident(g9,g10)
    c: Coincident(g10,g11)
    c: Coincident(g11,g12)
    c: Coincident(g12,g13)
    c: Coincident(g13,g14)
    c: PointOnObject(g14,g-2)
    c: Coincident(g14,g15)
    c: Coincident(g15,g3)
    c: Vertical(g15)
FEATURE [PartDesign::Revolution] Revolution001
  Angle = 360
  Axis = (0,1,0)
  Base = (0,0,0)
  Profile = -> Sketch038
  ReferenceAxis = -> Sketch038 [V_Axis]
FEATURE [PartDesign::Body] Body013  label="Body"
  Group = -> [Sketch038,Revolution001]
  Origin = -> Origin013
  Tip = -> Revolution001
FEATURE [Sketcher::SketchObject] Sketch039
  FullyConstrained = false
  MapMode = 5
  Placement = pos=(0,0,0) rot=(1,0,0;1.5708rad)
  Support = -> [XZ_Plane014]
  sketch-geometry (1):
    g0: Circle CenterX=-124.402 CenterY=0 CenterZ=0 NormalX=0 NormalY=0 NormalZ=1 AngleXU=0 Radius=14
  constraints (2):
    c: PointOnObject(g0,g-1)
    c: Diameter(g0) = 28
FEATURE [Sketcher::SketchObject] Sketch040
  AttachmentOffset = pos=(0,0,-2) rot=(0,0,1;0rad)
  FullyConstrained = false
  MapMode = 5
  Placement = pos=(0,2,4e-16) rot=(1,0,0;1.5708rad)
  Support = -> [XZ_Plane015]
  sketch-geometry (12):
    g0: LineSegment StartX=-80.6292 StartY=-33.8847 StartZ=0 EndX=-80.6292 EndY=-17 EndZ=0
    g1: LineSegment StartX=-75.7306 StartY=-25 StartZ=0 EndX=-75.7306 EndY=25 EndZ=0
    g2: LineSegment StartX=-135.759 StartY=17 StartZ=0 EndX=-80.6292 EndY=17 EndZ=0
    g3: LineSegment StartX=-80.6292 StartY=-17 StartZ=0 EndX=-135.759 EndY=-17 EndZ=0
    g4: LineSegment StartX=-135.759 StartY=-17 StartZ=0 EndX=-135.759 EndY=17 EndZ=0
    g5: LineSegment StartX=-80.6292 StartY=17 StartZ=0 EndX=-80.6292 EndY=33.8847 EndZ=0
    g6: Circle CenterX=-76.0392 CenterY=31 CenterZ=0 NormalX=0 NormalY=0 NormalZ=1 AngleXU=0 Radius=1.5
    g7: Circle CenterX=-76.0392 CenterY=-31 CenterZ=0 NormalX=0 NormalY=0 NormalZ=1 AngleXU=0 Radius=1.5
    g8: LineSegment StartX=-80.6292 StartY=33.8847 StartZ=0 EndX=-71.533 EndY=33.8847 EndZ=0
    g9: LineSegment StartX=-75.7306 StartY=25 StartZ=0 EndX=-71.533 EndY=33.8847 EndZ=0
    g10: LineSegment StartX=-80.6292 StartY=-33.8847 StartZ=0 EndX=-71.533 EndY=-33.8847 EndZ=0
    g11: LineSegment StartX=-75.7306 StartY=-25 StartZ=0 EndX=-71.533 EndY=-33.8847 EndZ=0
  constraints (31):
    c: Vertical(g1)
    c: Coincident(g3,g4)
    c: Coincident(g4,g2)
    c: Horizontal(g2)
    c: Horizontal(g3)
    c: Vertical(g4)
    c: DistanceY(g1,g1) = 50
    c: DistanceY(g1,g-1) = 25
    c: DistanceY(g3,g2) = 34
    c: Coincident(g5,g2)
    c: Coincident(g0,g3)
    c: Vertical(g7,g6)
    c: Equal(g6,g7)
    c: Diameter(g7) = 3
    c: DistanceY(g-1,g2) = 17
    c: Vertical(g0,g2)
    c: DistanceY(g7,g-1) = 31
    c: DistanceY(g-1,g6) = 31
    c: Equal(g0,g5)
    c: Vertical(g5)
    c: Vertical(g0)
    c: Coincident(g8,g5)
    c: Horizontal(g8)
    c: Coincident(g9,g1)
    c: Coincident(g9,g8)
    c: Coincident(g10,g0)
    c: Horizontal(g10)
    c: Coincident(g11,g1)
    c: Block(g6)
    c: Equal(g10,g8)
    c: Coincident(g10,g11)
FEATURE [PartDesign::Pad] Pad023
  Direction = (0,-1,-2e-16)
  Length = 29
  Length2 = 10
  Placement = pos=(0,0,0) rot=(1,0,0;1.5708rad)
  Profile = -> Sketch040
  ReferenceAxis = -> Sketch040 [N_Axis]
  Type = 0
FEATURE [Sketcher::SketchObject] Sketch041
  ExternalGeometry = -> [Pad023]
  FullyConstrained = true
  MapMode = 5
  Support = -> [XY_Plane015]
  sketch-geometry (4):
    g0: LineSegment StartX=-126.684 StartY=-27 StartZ=0 EndX=-116.129 EndY=2 EndZ=0
    g1: LineSegment StartX=-96.1844 StartY=-27 StartZ=0 EndX=-85.6292 EndY=2 EndZ=0
    g2: LineSegment StartX=-116.129 StartY=2 StartZ=0 EndX=-85.6292 EndY=2 EndZ=0
    g3: LineSegment StartX=-126.684 StartY=-27 StartZ=0 EndX=-96.1844 EndY=-27 EndZ=0
  constraints (12):
    c: PointOnObject(g0,g-4)
    c: PointOnObject(g0,g-3)
    c: Coincident(g2,g0)
    c: Coincident(g2,g1)
    c: Coincident(g3,g0)
    c: Coincident(g3,g1)
    c: Parallel(g0,g1)
    c: Angle(g-4,g1) = 1.22173
    c: PointOnObject(g1,g-3)
    c: Horizontal(g3)
    c: DistanceX(g1,g-6) = 5
    c: DistanceX(g2,g2) = 30.5
FEATURE [PartDesign::Pocket] Pocket016
  BaseFeature = -> Pad023
  Direction = (0,0,-1)
  Length = 28.2
  Length2 = 5
  Midplane = true
  Placement = pos=(0,0,0) rot=(1,0,0;1.5708rad)
  Profile = -> Sketch041
  ReferenceAxis = -> Sketch041 [N_Axis]
  Type = 0
FEATURE [Sketcher::SketchObject] Sketch042
  ExternalGeometry = -> [Pocket016]
  FullyConstrained = false
  MapMode = 5
  Support = -> [XY_Plane015]
  sketch-geometry (4):
    g0: LineSegment StartX=-80.6292 StartY=0 StartZ=0 EndX=-68.8 EndY=0 EndZ=0
    g1: LineSegment StartX=-68.8 StartY=0 StartZ=0 EndX=-68.8 EndY=-32.0908 EndZ=0
    g2: LineSegment StartX=-80.6292 StartY=0 StartZ=0 EndX=-80.6292 EndY=-32.0908 EndZ=0
    g3: LineSegment StartX=-80.6292 StartY=-32.0908 StartZ=0 EndX=-68.8 EndY=-32.0908 EndZ=0
  constraints (11):
    c: Coincident(g0,g1)
    c: Horizontal(g0)
    c: Vertical(g1)
    c: Coincident(g2,g0)
    c: Horizontal(g3)
    c: DistanceX(g0,g-1) = 68.8
    c: Coincident(g3,g1)
    c: PointOnObject(g0,g-1)
    c: Vertical(g2)
    c: Coincident(g2,g3)
    c: PointOnObject(g0,g-3)
FEATURE [PartDesign::Pocket] Pocket017
  BaseFeature = -> Pocket016
  Direction = (0,0,-1)
  Length = 5
  Length2 = 5
  Midplane = true
  Placement = pos=(0,0,0) rot=(1,0,0;1.5708rad)
  Profile = -> Sketch042
  ReferenceAxis = -> Sketch042 [N_Axis]
  Type = 1
FEATURE [PartDesign::Pad] Pad022
  Direction = (0,-1,-2e-16)
  Length = 150
  Length2 = 10
  Placement = pos=(0,0,0) rot=(1,0,0;1.5708rad)
  Profile = -> Sketch039
  ReferenceAxis = -> Sketch039 [N_Axis]
  Type = 0
FEATURE [PartDesign::Body] Body014
  Group = -> [Sketch039,Pad022]
  Origin = -> Origin014
  Placement = pos=(59.3183,76.4951,0) rot=(0,0,-1;0.354302rad)
  Tip = -> Pad022
FEATURE [PartDesign::Fillet] Fillet019
  Base = -> Pocket017 [Edge21,Edge34]
  BaseFeature = -> Pocket017
  Placement = pos=(0,0,0) rot=(1,0,0;1.5708rad)
  Radius = 11
  SupportTransform = false
  UseAllEdges = false
FEATURE [PartDesign::Body] Body015
  Group = -> [Sketch040,Pad023,Sketch041,Pocket016,Sketch042,Pocket017,Fillet019]
  Origin = -> Origin015
  Tip = -> Fillet019
FEATURE [Sketcher::SketchObject] Sketch043
  FullyConstrained = true
  MapMode = 5
  Support = -> [XY_Plane016]
  sketch-geometry (4):
    g0: LineSegment StartX=61 StartY=-28 StartZ=0 EndX=-139 EndY=-28 EndZ=0
    g1: LineSegment StartX=-139 StartY=-28 StartZ=0 EndX=-139 EndY=0 EndZ=0
    g2: LineSegment StartX=-139 StartY=0 StartZ=0 EndX=61 EndY=0 EndZ=0
    g3: LineSegment StartX=61 StartY=0 StartZ=0 EndX=61 EndY=-28 EndZ=0
  constraints (12):
    c: Coincident(g0,g1)
    c: Coincident(g1,g2)
    c: Coincident(g2,g3)
    c: Coincident(g3,g0)
    c: Horizontal(g0)
    c: Horizontal(g2)
    c: Vertical(g1)
    c: Vertical(g3)
    c: PointOnObject(g1,g-1)
    c: DistanceX(g0,g0) = 200
    c: DistanceY(g3,g3) = 28
    c: DistanceX(g-1,g0) = 61
FEATURE [PartDesign::Pad] Pad024
  Direction = (0,0,1)
  Length = 110
  Length2 = 10
  Midplane = true
  Profile = -> Sketch043
  ReferenceAxis = -> Sketch043 [N_Axis]
  Type = 0
FEATURE [Sketcher::SketchObject] Sketch044
  AttachmentOffset = pos=(0,0,3) rot=(0,0,1;0rad)
  ExternalGeometry = -> [Pad024]
  FullyConstrained = true
  MapMode = 5
  Placement = pos=(0,-3,-7e-16) rot=(1,0,0;1.5708rad)
  Support = -> [XZ_Plane016]
  sketch-geometry (16):
    g0: LineSegment StartX=-124 StartY=52 StartZ=0 EndX=-86 EndY=52 EndZ=0
    g1: LineSegment StartX=58 StartY=40 StartZ=0 EndX=58 EndY=-40 EndZ=0
    g2: LineSegment StartX=46 StartY=-52 StartZ=0 EndX=-83 EndY=-52 EndZ=0
    g3: LineSegment StartX=-136 StartY=-40 StartZ=0 EndX=-136 EndY=-22 EndZ=0
    g4: LineSegment StartX=-136 StartY=-22 StartZ=0 EndX=-86 EndY=-22 EndZ=0
    g5: LineSegment StartX=-86 StartY=-22 StartZ=0 EndX=-86 EndY=-52 EndZ=0
    g6: LineSegment StartX=-136 StartY=22 StartZ=0 EndX=-86 EndY=22 EndZ=0
    g7: LineSegment StartX=-86 StartY=22 StartZ=0 EndX=-86 EndY=52 EndZ=0
    g8: LineSegment StartX=-83 StartY=-52 StartZ=0 EndX=-83 EndY=52 EndZ=0
    g9: LineSegment StartX=-136 StartY=22 StartZ=0 EndX=-136 EndY=40 EndZ=0
    g10: LineSegment StartX=-86 StartY=-52 StartZ=0 EndX=-124 EndY=-52 EndZ=0
    g11: LineSegment StartX=-83 StartY=52 StartZ=0 EndX=46 EndY=52 EndZ=0
    g12: LineSegment StartX=-136 StartY=40 StartZ=0 EndX=-124 EndY=52 EndZ=0
    g13: LineSegment StartX=-136 StartY=-40 StartZ=0 EndX=-124 EndY=-52 EndZ=0
    g14: LineSegment StartX=46 StartY=-52 StartZ=0 EndX=58 EndY=-40 EndZ=0
    g15: LineSegment StartX=46 StartY=52 StartZ=0 EndX=58 EndY=40 EndZ=0
  constraints (48):
    c: Horizontal(g0)
    c: Horizontal(g2)
    c: Vertical(g1)
    c: Vertical(g3)
    c: Horizontal(g4)
    c: Coincident(g5,g4)
    c: Vertical(g5)
    c: Horizontal(g6)
    c: Coincident(g7,g6)
    c: Vertical(g7)
    c: Equal(g5,g7)
    c: Equal(g4,g6)
    c: DistanceY(g-1,g6) = 22
    c: Vertical(g8)
    c: DistanceX(g7,g8) = 3
    c: Coincident(g3,g4)
    c: Coincident(g9,g6)
    c: Coincident(g2,g8)
    c: Coincident(g10,g5)
    c: Coincident(g0,g7)
    c: Coincident(g11,g8)
    c: Vertical(g9)
    c: Angle(g9,g12) = 2.35619
    c: Angle(g10,g13) = 2.35619
    c: Angle(g1,g14) = 2.35619
    c: Angle(g11,g15) = 2.35619
    c: Horizontal(g11)
    c: Coincident(g9,g12)
    c: Coincident(g0,g12)
    c: Coincident(g3,g13)
    c: Coincident(g10,g13)
    c: Coincident(g2,g14)
    c: Coincident(g1,g14)
    c: Coincident(g11,g15)
    c: Coincident(g1,g15)
    c: DistanceX(g1,g-4) = 3
    c: DistanceY(g-4,g2) = 3
    c: Horizontal(g5,g2)
    c: Horizontal(g0,g8)
    c: DistanceY(g0,g-5) = 3
    c: DistanceX(g-5,g9) = 3
    c: Vertical(g3,g6)
    c: Horizontal(g10)
    c: Equal(g15,g12)
    c: Equal(g12,g13)
    c: Equal(g13,g14)
    c: DistanceX(g11,g11) = 129
    c: DistanceX(g0,g0) = 38
FEATURE [PartDesign::Pocket] Pocket018
  BaseFeature = -> Pad024
  Direction = (0,1,2e-16)
  Length = 0
  Length2 = 5
  Profile = -> Sketch044
  ReferenceAxis = -> Sketch044 [N_Axis]
  Reversed = true
  Type = 3
  UpToFace = -> Pad024 [Face1]
FEATURE [Sketcher::SketchObject] Sketch045
  FullyConstrained = false
  MapMode = 5
  Placement = pos=(0,0,0) rot=(1,0,0;1.5708rad)
  Support = -> [XZ_Plane016]
  sketch-geometry (8):
    g0: LineSegment StartX=-70.5644 StartY=30 StartZ=0 EndX=41.4356 EndY=30 EndZ=0
    g1: LineSegment StartX=41.4356 StartY=30 StartZ=0 EndX=41.4356 EndY=-30 EndZ=0
    g2: LineSegment StartX=41.4356 StartY=-30 StartZ=0 EndX=-70.5644 EndY=-30 EndZ=0
    g3: LineSegment StartX=-70.5644 StartY=-30 StartZ=0 EndX=-70.5644 EndY=30 EndZ=0
    g4: Circle CenterX=-76.0928 CenterY=31.0118 CenterZ=0 NormalX=0 NormalY=0 NormalZ=1 AngleXU=0 Radius=1.5
    g5: Circle CenterX=-76.0928 CenterY=-31.0259 CenterZ=0 NormalX=0 NormalY=0 NormalZ=1 AngleXU=0 Radius=1.5
    g6: Circle CenterX=46.05 CenterY=31.0118 CenterZ=0 NormalX=0 NormalY=0 NormalZ=1 AngleXU=0 Radius=1.5
    g7: Circle CenterX=46.05 CenterY=-31.0259 CenterZ=0 NormalX=0 NormalY=0 NormalZ=1 AngleXU=0 Radius=1.5
  constraints (22):
    c: Coincident(g0,g1)
    c: Coincident(g1,g2)
    c: Coincident(g2,g3)
    c: Coincident(g3,g0)
    c: Horizontal(g0)
    c: Horizontal(g2)
    c: Vertical(g1)
    c: Vertical(g3)
    c: DistanceY(g-1,g0) = 30
    c: DistanceY(g2,g-1) = 30
    c: DistanceX(g0,g0) = 112
    c: Equal(g7,g6)
    c: Equal(g7,g4)
    c: Equal(g7,g5)
    c: Diameter(g7) = 3
    c: Horizontal(g4,g6)
    c: Vertical(g4,g5)
    c: Horizontal(g5,g7)
    c: Vertical(g7,g6)
    c: Block(g6)
    c: Block(g4)
    c: Block(g5)
FEATURE [PartDesign::Pocket] Pocket019
  BaseFeature = -> Pocket018
  Direction = (0,1,2e-16)
  Length = 5
  Length2 = 5
  Midplane = true
  Profile = -> Sketch045
  ReferenceAxis = -> Sketch045 [N_Axis]
  Type = 1
FEATURE [Sketcher::SketchObject] Sketch046
  FullyConstrained = true
  MapMode = 5
  Support = -> [XY_Plane016]
  sketch-geometry (4):
    g0: LineSegment StartX=-129.522 StartY=-29.7081 StartZ=0 EndX=-116.009 EndY=7.41876 EndZ=0
    g1: LineSegment StartX=-99.5219 StartY=-29.7081 StartZ=0 EndX=-86.0088 EndY=7.41876 EndZ=0
    g2: LineSegment StartX=-129.522 StartY=-29.7081 StartZ=0 EndX=-99.5219 EndY=-29.7081 EndZ=0
    g3: LineSegment StartX=-116.009 StartY=7.41876 StartZ=0 EndX=-86.0088 EndY=7.41876 EndZ=0
  constraints (10):
    c: Coincident(g2,g0)
    c: Coincident(g2,g1)
    c: Horizontal(g2)
    c: Angle(g2,g0) = 1.22173
    c: Angle(g1,g2) = 1.91986
    c: Coincident(g3,g0)
    c: Coincident(g3,g1)
    c: Horizontal(g3)
    c: Block(g0)
    c: DistanceX(g3,g3) = 30
FEATURE [PartDesign::Pocket] Pocket020
  BaseFeature = -> Pocket019
  Direction = (0,0,-1)
  Length = 28
  Length2 = 5
  Midplane = true
  Profile = -> Sketch046
  ReferenceAxis = -> Sketch046 [N_Axis]
  Type = 0
FEATURE [PartDesign::Fillet] Fillet020
  Base = -> Pocket020 [Edge27,Edge26,Edge30,Edge28]
  BaseFeature = -> Pocket020
  Radius = 10
  SupportTransform = false
  UseAllEdges = false
FEATURE [Sketcher::SketchObject] Sketch047
  AttachmentOffset = pos=(0,0,10) rot=(0,0,1;0rad)
  ExternalGeometry = -> [Fillet020]
  FullyConstrained = true
  MapMode = 5
  Placement = pos=(0,-10,-2.2e-15) rot=(1,0,0;1.5708rad)
  Support = -> [XZ_Plane016]
  sketch-geometry (4):
    g0: Circle CenterX=-133 CenterY=49 CenterZ=0 NormalX=0 NormalY=0 NormalZ=1 AngleXU=0 Radius=1.5
    g1: Circle CenterX=-133 CenterY=-49 CenterZ=0 NormalX=0 NormalY=0 NormalZ=1 AngleXU=0 Radius=1.5
    g2: Circle CenterX=55 CenterY=-49 CenterZ=0 NormalX=0 NormalY=0 NormalZ=1 AngleXU=0 Radius=1.5
    g3: Circle CenterX=55 CenterY=49 CenterZ=0 NormalX=0 NormalY=0 NormalZ=1 AngleXU=0 Radius=1.5
  constraints (12):
    c: Diameter(g3) = 3
    c: Equal(g0,g3)
    c: Equal(g3,g2)
    c: Equal(g2,g1)
    c: Vertical(g0,g1)
    c: Horizontal(g0,g3)
    c: Vertical(g3,g2)
    c: Horizontal(g1,g2)
    c: DistanceY(g0,g-3) = 3
    c: DistanceX(g-3,g0) = 3
    c: DistanceY(g-4,g1) = 3
    c: DistanceX(g2,g-5) = 3
FEATURE [PartDesign::Pocket] Pocket021
  BaseFeature = -> Fillet020
  Direction = (0,1,2e-16)
  Length = 0
  Length2 = 5
  Profile = -> Sketch047
  ReferenceAxis = -> Sketch047 [N_Axis]
  Type = 3
  UpToFace = -> Fillet020 [Face1]
FEATURE [Sketcher::SketchObject] Sketch048
  ExternalGeometry = -> [Pocket021]
  FullyConstrained = false
  MapMode = 5
  Placement = pos=(0,0,0) rot=(1,0,0;1.5708rad)
  Support = -> [XZ_Plane016]
  sketch-geometry (4):
    g0: LineSegment StartX=-120.595 StartY=44.7295 StartZ=0 EndX=-101.595 EndY=44.7295 EndZ=0
    g1: LineSegment StartX=-101.595 StartY=44.7295 StartZ=0 EndX=-101.595 EndY=32.2295 EndZ=0
    g2: LineSegment StartX=-101.595 StartY=32.2295 StartZ=0 EndX=-120.595 EndY=32.2295 EndZ=0
    g3: LineSegment StartX=-120.595 StartY=32.2295 StartZ=0 EndX=-120.595 EndY=44.7295 EndZ=0
  constraints (10):
    c: Coincident(g0,g1)
    c: Coincident(g1,g2)
    c: Coincident(g2,g3)
    c: Coincident(g3,g0)
    c: Horizontal(g0)
    c: Horizontal(g2)
    c: Vertical(g1)
    c: Vertical(g3)
    c: DistanceX(g0,g0) = 19
    c: DistanceY(g1,g1) = 12.5
FEATURE [PartDesign::Pocket] Pocket022
  BaseFeature = -> Pocket021
  Direction = (0,1,2e-16)
  Length = 5
  Length2 = 5
  Profile = -> Sketch048
  ReferenceAxis = -> Sketch048 [N_Axis]
  Reversed = true
  Type = 1
FEATURE [Sketcher::SketchObject] Sketch049
  AttachmentOffset = pos=(0,0,13) rot=(0,0,1;0rad)
  FullyConstrained = false
  MapMode = 5
  Placement = pos=(0,-13,-2.9e-15) rot=(1,0,0;1.5708rad)
  Support = -> [XZ_Plane016]
  sketch-geometry (4):
    g0: LineSegment StartX=-88.4656 StartY=46.3382 StartZ=0 EndX=-80.4395 EndY=46.3382 EndZ=0
    g1: LineSegment StartX=-80.4395 StartY=46.3382 StartZ=0 EndX=-80.4395 EndY=30.8062 EndZ=0
    g2: LineSegment StartX=-80.4395 StartY=30.8062 StartZ=0 EndX=-88.4656 EndY=30.8062 EndZ=0
    g3: LineSegment StartX=-88.4656 StartY=30.8062 StartZ=0 EndX=-88.4656 EndY=46.3382 EndZ=0
  constraints (8):
    c: Coincident(g0,g1)
    c: Coincident(g1,g2)
    c: Coincident(g2,g3)
    c: Coincident(g3,g0)
    c: Horizontal(g0)
    c: Horizontal(g2)
    c: Vertical(g1)
    c: Vertical(g3)
FEATURE [PartDesign::Pocket] Pocket023
  BaseFeature = -> Pocket022
  Direction = (0,1,2e-16)
  Length = 5
  Length2 = 5
  Profile = -> Sketch049
  ReferenceAxis = -> Sketch049 [N_Axis]
  Reversed = true
  Type = 1
FEATURE [PartDesign::Body] Body016
  Group = -> [Sketch043,Pad024,Sketch044,Pocket018,Sketch045,Pocket019,Sketch046,Pocket020,Fillet020,Sketch047,Pocket021,Sketch048,Pocket022,Sketch049,Pocket023]
  Origin = -> Origin016
  Placement = pos=(0,-5.08,0) rot=(0,0,1;0rad)
  Tip = -> Pocket023
